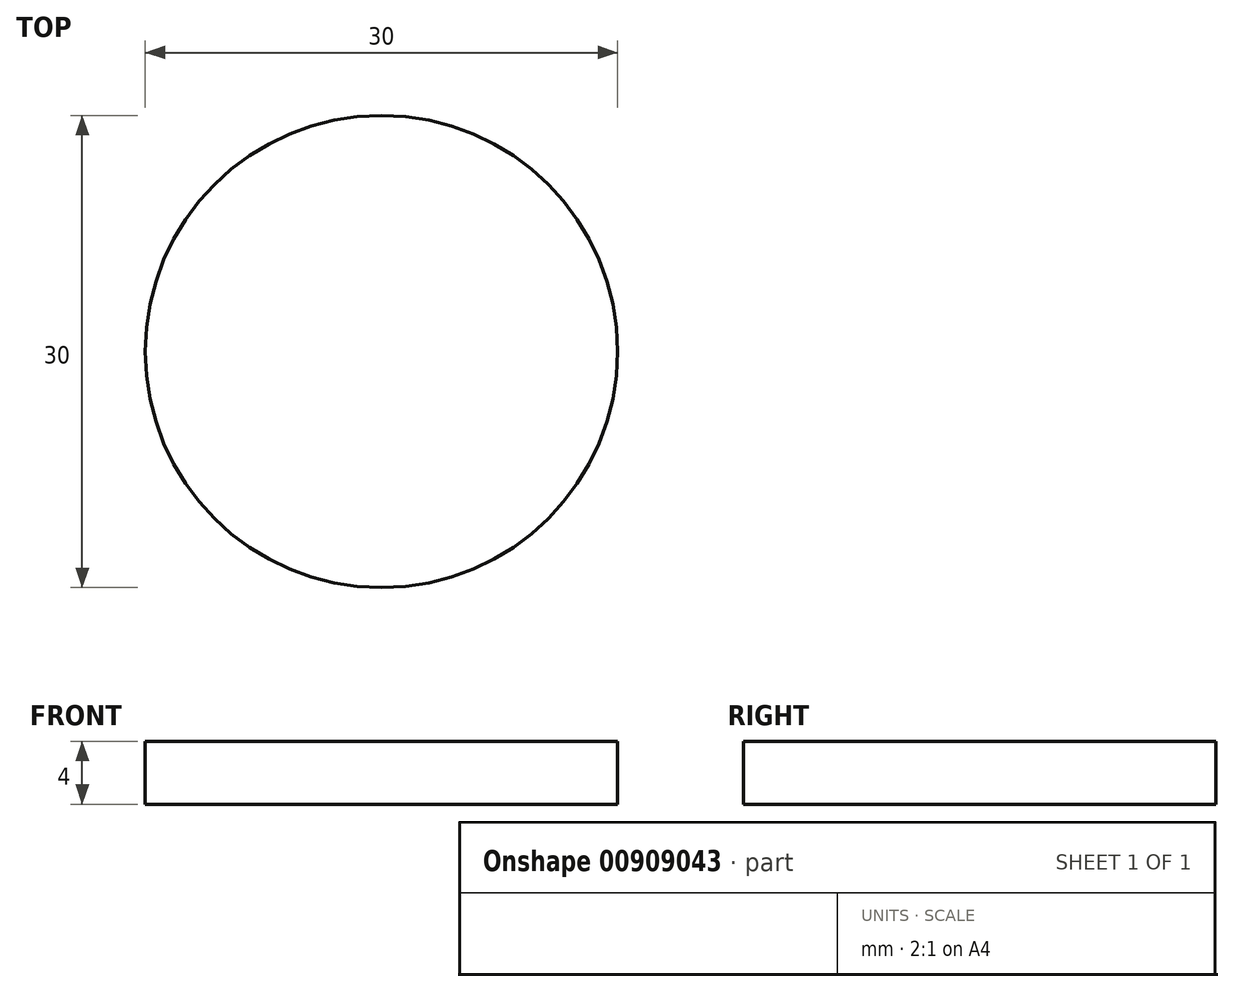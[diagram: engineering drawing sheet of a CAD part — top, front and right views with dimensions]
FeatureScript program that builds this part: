
annotation { "Feature Type Name" : "Feature", "Feature Type Description" : "" }
export const myFeature = defineFeature(function(context is Context, id is Id, definition is map)
    precondition{}
    {
        {
            var Q0;
            Q0=qCreatedBy(makeId("Top.planeOp"),FACE);
            var sketch = newSketch(context, id + "F0", { "sketchPlane" : qUnion([Q0])});
            skCircle(sketch, "E0", {"center": v(0, 0) * mm, "radius": 15 * mm});
            skSolve(sketch);
        }
        {
            var Q0;
            Q0=makeQuery(id+"F0.imprint","IMPRINT",FACE,{"disambiguationData":[TD([[makeQuery(id+"F0.imprint","IMPRINT",EDGE,{"derivedFrom":sQuery(id+"F0.wireOp",EDGE,"E0")}),1.0]])]});
            extrude(context, id + "F1", {"entities" : qUnion([Q0]), "depth" : 4 * mm, "offsetDistance" : 25 * mm});
        }
    });
